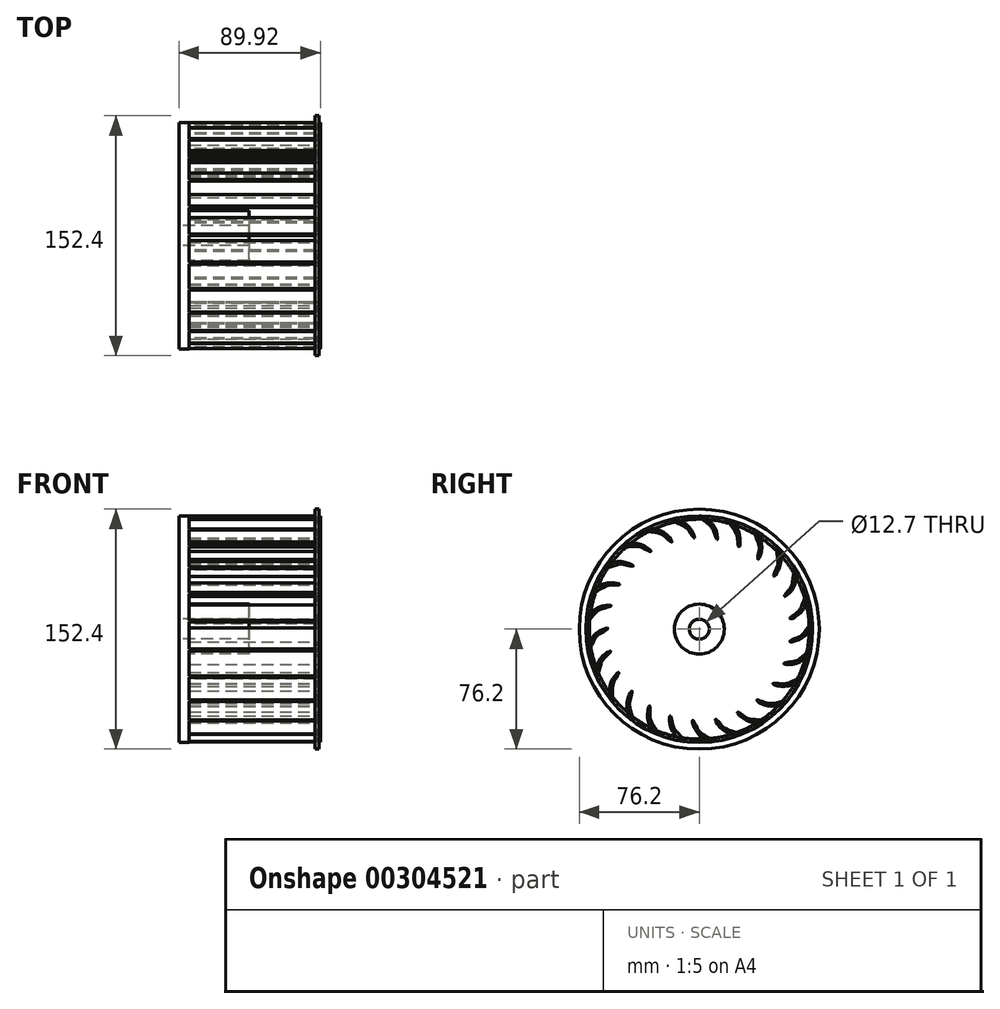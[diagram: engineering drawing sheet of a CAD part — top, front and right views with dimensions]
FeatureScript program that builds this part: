
annotation { "Feature Type Name" : "Feature", "Feature Type Description" : "" }
export const myFeature = defineFeature(function(context is Context, id is Id, definition is map)
    precondition{}
    {
        {
            var Q0;
            Q0=qCreatedBy(makeId("Right.planeOp"),FACE);
            var sketch = newSketch(context, id + "F0", { "sketchPlane" : qUnion([Q0])});
            skCircle(sketch, "E0", {"center": v(0, 0) * mm, "radius": 71.9 * mm});
            skCircle(sketch, "E1", {"center": v(0, 0) * mm, "radius": 6.35 * mm});
            skCircle(sketch, "E2", {"center": v(0, 0) * mm, "radius": 15.88 * mm});
            skSolve(sketch);
        }
        {
            var Q0;
            Q0 = qSketchRegion(id + "F0", true);
            extrude(context, id + "F1", {"entities" : qUnion([Q0]), "depth" : 12.7 * mm});
        }
        {
            var Q0;
            Q0=makeQuery(id+"F0.imprint","IMPRINT",FACE,{"disambiguationData":[TD([[makeQuery(id+"F0.imprint","IMPRINT",EDGE,{"derivedFrom":sQuery(id+"F0.wireOp",EDGE,"E1")}),-1.0]])]});
            extrude(context, id + "F2", {"entities" : qUnion([Q0]), "operationType" : NewBodyOperationType.ADD, "depth" : 50.8 * mm});
        }
        {
            var Q0;
            Q0=makeQuery(id+"F1.opExtrude","CAP_FACE",FACE,{"disambiguationData":[OSD([sQuery(id+"F0.wireOp",EDGE,"E0"),sQuery(id+"F0.wireOp",EDGE,"E2")])],"isStart":false});
            var sketch = newSketch(context, id + "F3", { "sketchPlane" : qUnion([Q0])});
            skFitSpline(sketch, "E3", {"points": [v(0, 71.9) * mm, v(8.57, 66.59) * mm, v(11.42, 56.88) * mm, v(9.6, 60.89) * mm, v(7.18, 65.43) * mm, v(0, 71.9) * mm]});
            skSolve(sketch);
        }
        {
            var Q0;
            {var subQ0=sQuery(id+"F3.wireOp",EDGE,"E3");var subQ1=makeQuery(id+"F1.opExtrude","CAP_EDGE",EDGE,{"disambiguationData":[OSD([sQuery(id+"F0.wireOp",EDGE,"E0")])],"isStart":false});var subQ2=makeQuery(id+"F3.imprint","INTERSECT",VERTEX,{"disambiguationData":[OD(0.0)],"derivedFrom":[subQ1,subQ0]});Q0=makeQuery(id+"F3.imprint","IMPRINT",FACE,{"disambiguationData":[TD([[makeQuery(id+"F3.imprint","IMPRINT",EDGE,{"disambiguationData":[TD([[subQ2,1.0]])],"derivedFrom":subQ0}),-1.0]])]});}
            extrude(context, id + "F4", {"entities" : qUnion([Q0]), "operationType" : NewBodyOperationType.ADD, "depth" : 83.32 * mm});
        }
        {
            var Q0;
            Q0=makeQuery(id+"F4.opExtrude","SWEPT_FACE",FACE,{"disambiguationData":[OSD([sQuery(id+"F3.wireOp",EDGE,"E3")])]});
            var Q1;
            Q1=makeQuery(id+"F4.opExtrude","CAP_FACE",FACE,{"disambiguationData":[OSD([sQuery(id+"F0.wireOp",EDGE,"E0"),sQuery(id+"F3.wireOp",EDGE,"E3")])],"isStart":false});
            var Q2;
            Q2=makeQuery(id+"F2.opExtrude","SWEPT_FACE",FACE,{"disambiguationData":[OSD([sQuery(id+"F0.wireOp",EDGE,"E1")])]});
            circularPattern(context, id + "F5", {"patternType" : PatternType.FACE, "faces" : qUnion([Q0, Q1]), "axis" : qUnion([Q2]), "angle" : 360 * degree, "instanceCount" : 25, "equalSpace" : true});
        }
        {
            var Q0;
            Q0=makeQuery(id+"F4.opExtrude","CAP_FACE",FACE,{"disambiguationData":[OSD([sQuery(id+"F0.wireOp",EDGE,"E0"),sQuery(id+"F3.wireOp",EDGE,"E3")])],"isStart":false});
            var sketch = newSketch(context, id + "F6", { "sketchPlane" : qUnion([Q0])});
            skCircle(sketch, "E4", {"center": v(0, 0) * mm, "radius": 71.9 * mm});
            skCircle(sketch, "E5", {"center": v(0, 0) * mm, "radius": 59.7 * mm});
            skSolve(sketch);
        }
        {
            var Q0;
            Q0=makeQuery(id+"F0.imprint","IMPRINT",FACE,{"disambiguationData":[TD([[makeQuery(id+"F0.imprint","IMPRINT",EDGE,{"derivedFrom":sQuery(id+"F0.wireOp",EDGE,"E0")}),1.0]])]});
            var sketch = newSketch(context, id + "F7", { "sketchPlane" : qUnion([Q0])});
            skLineSegment(sketch, "E6.bottom", {"start": v(-3.07, 3.8) * mm, "end": v(3.07, 3.8) * mm});
            skLineSegment(sketch, "E6.top", {"start": v(-3.07, 17.05) * mm, "end": v(3.07, 17.05) * mm});
            skLineSegment(sketch, "E6.left", {"start": v(-3.07, 3.8) * mm, "end": v(-3.07, 17.05) * mm});
            skLineSegment(sketch, "E6.right", {"start": v(3.07, 3.8) * mm, "end": v(3.07, 17.05) * mm});
            skPoint(sketch, "E6.middle", {"position": v(0, 10.43) * mm});
            skSolve(sketch);
        }
        {
            var Q0;
            Q0=qCreatedBy(makeId("Top.planeOp"),FACE);
            var sketch = newSketch(context, id + "F8", { "sketchPlane" : qUnion([Q0])});
            skCircle(sketch, "E7", {"center": v(-15.99, 26.82) * mm, "radius": 4.42 * mm});
            skLineSegment(sketch, "E8", {"start": v(92.7, 76.2) * mm, "end": v(95.25, 76.2) * mm});
            skLineSegment(sketch, "E9", {"start": v(95.25, 76.2) * mm, "end": v(95.25, 72) * mm});
            skLineSegment(sketch, "E10", {"start": v(95.25, 72) * mm, "end": v(92.71, 69.85) * mm});
            skLineSegment(sketch, "E11", {"start": v(92.7, 69.85) * mm, "end": v(92.7, 76.2) * mm});
            skSolve(sketch);
        }
        {
            var Q0;
            Q0 = qSketchRegion(id + "F8", true);
            var Q1;
            Q1=makeQuery(id+"F2.opExtrude","SWEPT_FACE",FACE,{"disambiguationData":[OSD([sQuery(id+"F0.wireOp",EDGE,"E1")])]});
            revolve(context, id + "F9", {"operationType" : NewBodyOperationType.REMOVE, "entities" : qUnion([Q0]), "axis" : qUnion([Q1]), "revolveType" : RevolveType.FULL, "oppositeDirection" : true});
        }
        {
            var Q0;
            Q0=makeQuery(id+"F8.imprint","IMPRINT",FACE,{"disambiguationData":[TD([[makeQuery(id+"F8.imprint","IMPRINT",EDGE,{"derivedFrom":sQuery(id+"F8.wireOp",EDGE,"E8")}),-1.0]])]});
            var Q1;
            Q1=makeQuery(id+"F2.opExtrude","SWEPT_FACE",FACE,{"disambiguationData":[OSD([sQuery(id+"F0.wireOp",EDGE,"E1")])]});
            revolve(context, id + "F10", {"entities" : qUnion([Q0]), "axis" : qUnion([Q1]), "revolveType" : RevolveType.FULL});
        }
        {
            var Q0;
            {var subQ0=sQuery(id+"F0.wireOp",EDGE,"E2");Q0=makeQuery(id+"F2.boolean.opBoolean","MERGE",FACE,{"derivedFrom":[makeQuery(id+"F1.opExtrude","CAP_FACE",FACE,{"disambiguationData":[OSD([sQuery(id+"F0.wireOp",EDGE,"E0"),subQ0])],"isStart":true}),makeQuery(id+"F2.opExtrude","CAP_FACE",FACE,{"disambiguationData":[OSD([sQuery(id+"F0.wireOp",EDGE,"E1"),subQ0])],"isStart":true})]});}
            extrude(context, id + "F11", {"entities" : qUnion([Q0]), "operationType" : NewBodyOperationType.REMOVE, "oppositeDirection" : true, "depth" : 6.1 * mm});
        }
    });
